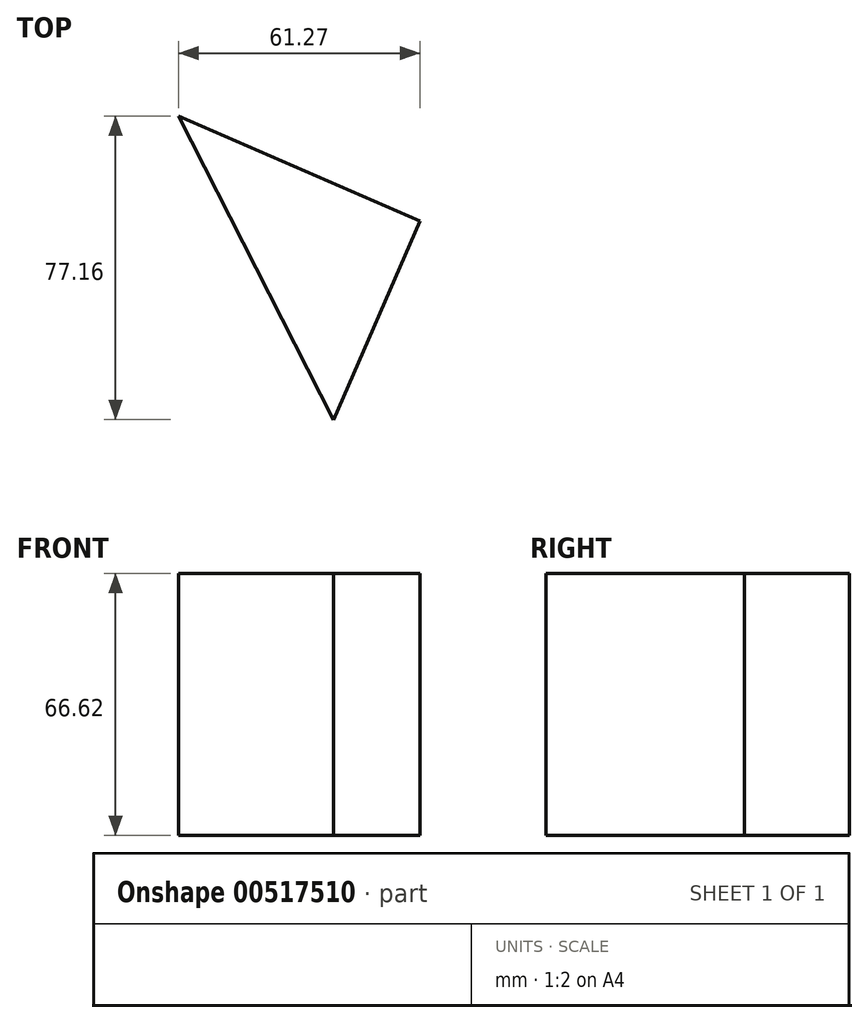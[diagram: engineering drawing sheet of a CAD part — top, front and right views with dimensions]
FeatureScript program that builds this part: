
annotation { "Feature Type Name" : "Feature", "Feature Type Description" : "" }
export const myFeature = defineFeature(function(context is Context, id is Id, definition is map)
    precondition{}
    {
        {
            var Q0;
            Q0=qCreatedBy(makeId("Top.planeOp"),FACE);
            var sketch = newSketch(context, id + "F0", { "sketchPlane" : qUnion([Q0])});
            skLineSegment(sketch, "E0", {"start": v(-21.42, 38.9) * mm, "end": v(39.85, 12.27) * mm});
            skLineSegment(sketch, "E1", {"start": v(39.85, 12.27) * mm, "end": v(17.89, -38.26) * mm});
            skLineSegment(sketch, "E2", {"start": v(17.89, -38.26) * mm, "end": v(-21.42, 38.9) * mm});
            skSolve(sketch);
        }
        {
            var Q0;
            Q0=makeQuery(id+"F0.imprint","IMPRINT",FACE,{"disambiguationData":[TD([[makeQuery(id+"F0.imprint","IMPRINT",EDGE,{"derivedFrom":sQuery(id+"F0.wireOp",EDGE,"E0")}),-1.0]])]});
            extrude(context, id + "F1", {"entities" : qUnion([Q0]), "depth" : 66.62 * mm, "offsetDistance" : 25.4 * mm});
        }
    });
